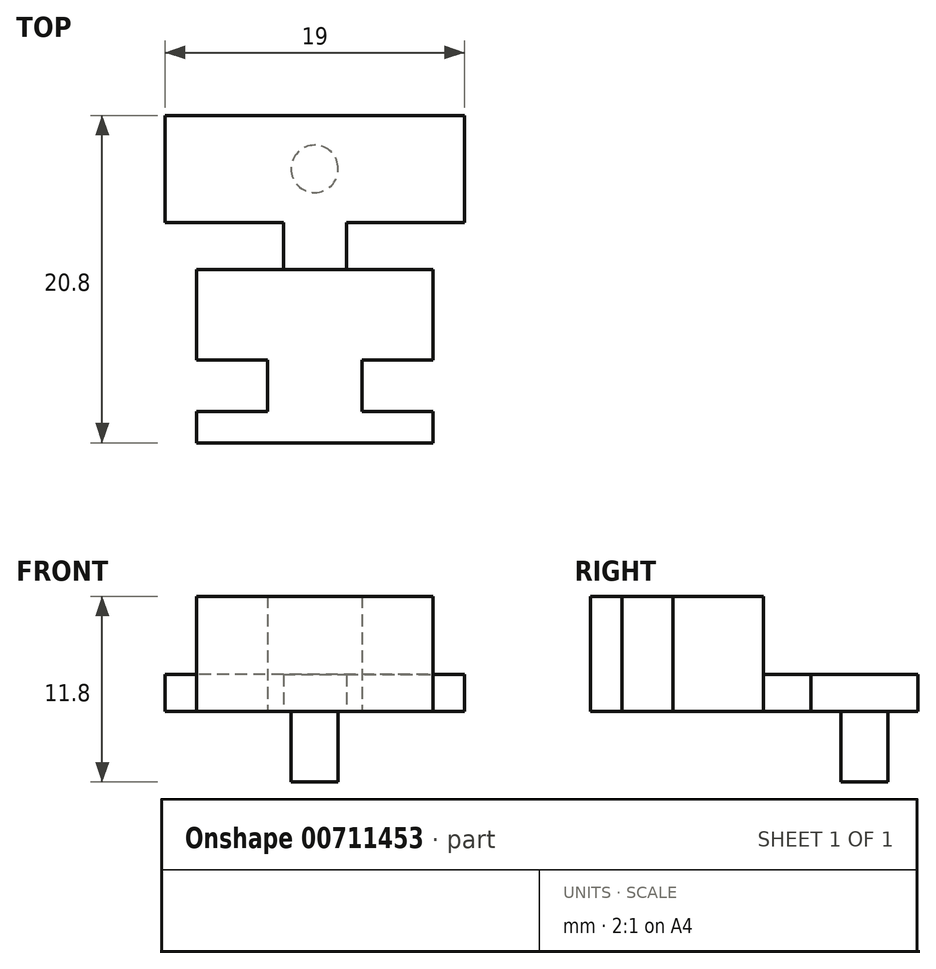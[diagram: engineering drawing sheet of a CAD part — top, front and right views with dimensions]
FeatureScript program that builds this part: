
annotation { "Feature Type Name" : "Feature", "Feature Type Description" : "" }
export const myFeature = defineFeature(function(context is Context, id is Id, definition is map)
    precondition{}
    {
        {
            var Q0;
            Q0=qCreatedBy(makeId("Top.planeOp"),FACE);
            var sketch = newSketch(context, id + "F0", { "sketchPlane" : qUnion([Q0])});
            skLineSegment(sketch, "E0.bottom", {"start": v(-9.84, 10.17) * mm, "end": v(5.16, 10.17) * mm});
            skLineSegment(sketch, "E0.top", {"start": v(-9.84, -0.83) * mm, "end": v(5.16, -0.83) * mm});
            skLineSegment(sketch, "E0.left", {"start": v(-9.84, 10.17) * mm, "end": v(-9.84, 4.42) * mm});
            skLineSegment(sketch, "E0.right", {"start": v(5.16, 10.17) * mm, "end": v(5.16, 4.42) * mm});
            skPoint(sketch, "E1", {"position": v(-2.34, 10.17) * mm});
            skLineSegment(sketch, "E2.bottom", {"start": v(-4.34, 10.17) * mm, "end": v(-0.34, 10.17) * mm});
            skLineSegment(sketch, "E2.top", {"start": v(-4.34, 13.17) * mm, "end": v(-0.34, 13.17) * mm});
            skLineSegment(sketch, "E2.left", {"start": v(-4.34, 10.17) * mm, "end": v(-4.34, 13.17) * mm});
            skLineSegment(sketch, "E2.right", {"start": v(-0.34, 10.17) * mm, "end": v(-0.34, 13.17) * mm});
            skLineSegment(sketch, "E3.bottom", {"start": v(-2.34, 13.17) * mm, "end": v(-11.84, 13.17) * mm});
            skLineSegment(sketch, "E3.top", {"start": v(-2.34, 19.97) * mm, "end": v(-11.84, 19.97) * mm});
            skLineSegment(sketch, "E3.left", {"start": v(-2.34, 13.17) * mm, "end": v(-2.34, 19.97) * mm});
            skLineSegment(sketch, "E3.right", {"start": v(-11.84, 13.17) * mm, "end": v(-11.84, 19.97) * mm});
            skLineSegment(sketch, "E4.MirrorCS", {"start": v(-2.34, 13.17) * mm, "end": v(7.16, 13.17) * mm});
            skLineSegment(sketch, "E5.MirrorCS", {"start": v(7.16, 13.17) * mm, "end": v(7.16, 19.97) * mm});
            skLineSegment(sketch, "E6.MirrorCS", {"start": v(-2.34, 19.97) * mm, "end": v(7.16, 19.97) * mm});
            skLineSegment(sketch, "E7.bottom", {"start": v(-9.84, 4.42) * mm, "end": v(-5.34, 4.42) * mm});
            skLineSegment(sketch, "E7.top", {"start": v(-9.84, 1.17) * mm, "end": v(-5.34, 1.17) * mm});
            skLineSegment(sketch, "E7.right", {"start": v(-5.34, 4.42) * mm, "end": v(-5.34, 1.17) * mm});
            skLineSegment(sketch, "E8", {"start": v(-2.34, 10.17) * mm, "end": v(-2.34, -0.83) * mm, "construction": true});
            skLineSegment(sketch, "E9.trimOffspring", {"start": v(-9.84, 1.17) * mm, "end": v(-9.84, -0.83) * mm});
            skLineSegment(sketch, "E10.MirrorCS", {"start": v(0.66, 4.42) * mm, "end": v(0.66, 1.17) * mm});
            skLineSegment(sketch, "E11.MirrorCS", {"start": v(5.16, 4.42) * mm, "end": v(0.66, 4.42) * mm});
            skLineSegment(sketch, "E12.MirrorCS", {"start": v(5.16, 1.17) * mm, "end": v(0.66, 1.17) * mm});
            skLineSegment(sketch, "E13.trimOffspring", {"start": v(5.16, 1.17) * mm, "end": v(5.16, -0.83) * mm});
            skSolve(sketch);
        }
        {
            var Q0;
            {var subQ1=sQuery(id+"F0.wireOp",EDGE,"E3.bottom");Q0=makeQuery(id+"F0.imprint","IMPRINT",FACE,{"disambiguationData":[TD([[makeQuery(id+"F0.imprint","IMPRINT",EDGE,{"derivedFrom":subQ1}),-1.0]])]});}
            var Q1;
            {var subQ1=sQuery(id+"F0.wireOp",EDGE,"E3.left");Q1=makeQuery(id+"F0.imprint","IMPRINT",FACE,{"disambiguationData":[TD([[makeQuery(id+"F0.imprint","IMPRINT",EDGE,{"derivedFrom":subQ1}),-1.0]])]});}
            var Q2;
            {var subQ0=sQuery(id+"F0.wireOp",EDGE,"E2.left");Q2=makeQuery(id+"F0.imprint","IMPRINT",FACE,{"disambiguationData":[TD([[makeQuery(id+"F0.imprint","IMPRINT",EDGE,{"derivedFrom":subQ0}),-1.0]])]});}
            extrude(context, id + "F1", {"entities" : qUnion([Q0, Q1, Q2]), "depth" : 2.34 * mm, "offsetDistance" : 25 * mm});
        }
        {
            var Q0;
            Q0=makeQuery(id+"F0.imprint","IMPRINT",FACE,{"disambiguationData":[TD([[makeQuery(id+"F0.imprint","IMPRINT",EDGE,{"derivedFrom":sQuery(id+"F0.wireOp",EDGE,"E0.top")}),1.0]])]});
            extrude(context, id + "F2", {"entities" : qUnion([Q0]), "operationType" : NewBodyOperationType.ADD, "depth" : 7.3 * mm, "offsetDistance" : 25 * mm});
        }
        {
            var Q0;
            {var subQ0=sQuery(id+"F0.wireOp",EDGE,"E0.bottom");Q0=makeQuery(id+"F2.boolean.opBoolean","MERGE",FACE,{"derivedFrom":[makeQuery(id+"F1.opExtrude","CAP_FACE",FACE,{"disambiguationData":[OSD([subQ0,sQuery(id+"F0.wireOp",EDGE,"E2.left"),sQuery(id+"F0.wireOp",EDGE,"E2.right"),sQuery(id+"F0.wireOp",EDGE,"E3.bottom"),sQuery(id+"F0.wireOp",EDGE,"E3.top"),sQuery(id+"F0.wireOp",EDGE,"E3.right"),sQuery(id+"F0.wireOp",EDGE,"E4.MirrorCS"),sQuery(id+"F0.wireOp",EDGE,"E5.MirrorCS"),sQuery(id+"F0.wireOp",EDGE,"E6.MirrorCS")])],"isStart":true}),makeQuery(id+"F2.opExtrude","CAP_FACE",FACE,{"disambiguationData":[OSD([subQ0,sQuery(id+"F0.wireOp",EDGE,"E0.top"),sQuery(id+"F0.wireOp",EDGE,"E0.left"),sQuery(id+"F0.wireOp",EDGE,"E0.right"),sQuery(id+"F0.wireOp",EDGE,"E7.bottom"),sQuery(id+"F0.wireOp",EDGE,"E7.top"),sQuery(id+"F0.wireOp",EDGE,"E7.right"),sQuery(id+"F0.wireOp",EDGE,"E9.trimOffspring"),sQuery(id+"F0.wireOp",EDGE,"E10.MirrorCS"),sQuery(id+"F0.wireOp",EDGE,"E11.MirrorCS"),sQuery(id+"F0.wireOp",EDGE,"E12.MirrorCS"),sQuery(id+"F0.wireOp",EDGE,"E13.trimOffspring")])],"isStart":true})]});}
            var sketch = newSketch(context, id + "F3", { "sketchPlane" : qUnion([Q0])});
            skCircle(sketch, "E14", {"center": v(-2.35, -16.57) * mm, "radius": 1.5 * mm});
            skSolve(sketch);
        }
        {
            var Q0;
            Q0 = qSketchRegion(id + "F3", true);
            extrude(context, id + "F4", {"entities" : qUnion([Q0]), "operationType" : NewBodyOperationType.ADD, "depth" : 4.5 * mm, "offsetDistance" : 25 * mm});
        }
    });
